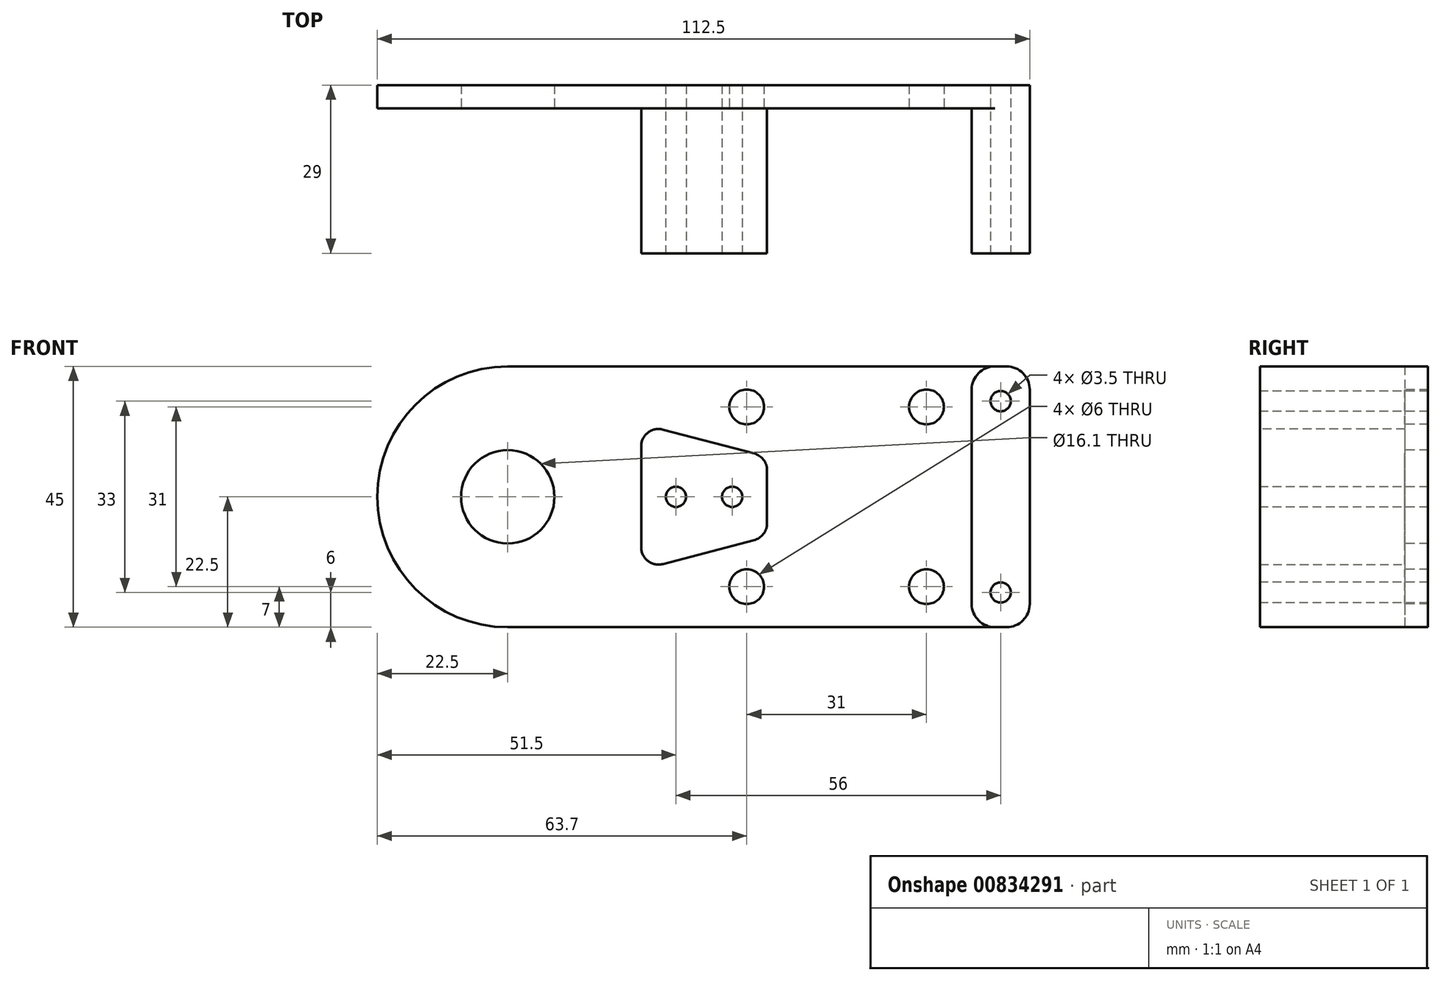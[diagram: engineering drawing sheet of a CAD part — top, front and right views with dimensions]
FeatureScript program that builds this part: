
annotation { "Feature Type Name" : "Feature", "Feature Type Description" : "" }
export const myFeature = defineFeature(function(context is Context, id is Id, definition is map)
    precondition{}
    {
        {
            var Q0;
            Q0=qCreatedBy(makeId("Front.planeOp"),FACE);
            var sketch = newSketch(context, id + "F0", { "sketchPlane" : qUnion([Q0])});
            skLineSegment(sketch, "E0.bottom", {"start": v(-45, 22.5) * mm, "end": v(45, 22.5) * mm});
            skLineSegment(sketch, "E0.top", {"start": v(-45, -22.5) * mm, "end": v(45, -22.5) * mm});
            skLineSegment(sketch, "E0.right", {"start": v(45, 22.5) * mm, "end": v(45, -22.5) * mm});
            skPoint(sketch, "E0.middle", {"position": v(0, 0) * mm});
            skArc(sketch, "E1", {"start": v(-45, 22.5) * mm, "mid": v(-67.5, 0) * mm, "end": v(-45, -22.5) * mm});
            skSolve(sketch);
        }
        {
            var Q0;
            Q0=qSketchRegion(id+"F0",true);
            extrude(context, id + "F1", {"entities" : qUnion([Q0]), "depth" : 4 * mm, "offsetDistance" : 25 * mm});
        }
        {
            var Q0;
            Q0=makeQuery(id+"F1.opExtrude","CAP_FACE",FACE,{"disambiguationData":[OSD([sQuery(id+"F0.wireOp",EDGE,"E0.bottom"),sQuery(id+"F0.wireOp",EDGE,"E0.top"),sQuery(id+"F0.wireOp",EDGE,"E0.right"),sQuery(id+"F0.wireOp",EDGE,"E1")])],"isStart":false});
            var sketch = newSketch(context, id + "F2", { "sketchPlane" : qUnion([Q0])});
            skCircle(sketch, "E2", {"center": v(-45, 0) * mm, "radius": 8.05 * mm});
            skSolve(sketch);
        }
        {
            var Q0;
            Q0 = qSketchRegion(id + "F2", true);
            extrude(context, id + "F3", {"entities" : qUnion([Q0]), "operationType" : NewBodyOperationType.REMOVE, "endBound" : BoundingType.THROUGH_ALL, "oppositeDirection" : true, "depth" : 25 * mm, "offsetDistance" : 25 * mm});
        }
        {
            var Q0;
            Q0=makeQuery(id+"F1.opExtrude","CAP_FACE",FACE,{"disambiguationData":[OSD([sQuery(id+"F0.wireOp",EDGE,"E0.bottom"),sQuery(id+"F0.wireOp",EDGE,"E0.top"),sQuery(id+"F0.wireOp",EDGE,"E0.right"),sQuery(id+"F0.wireOp",EDGE,"E1")])],"isStart":false});
            var sketch = newSketch(context, id + "F4", { "sketchPlane" : qUnion([Q0])});
            skCircle(sketch, "E3", {"center": v(-45, 0) * mm, "radius": 19.1 * mm, "construction": true});
            skLineSegment(sketch, "E4", {"start": v(-45, 0) * mm, "end": v(11.7, 0) * mm, "construction": true});
            skCircle(sketch, "E5", {"center": v(11.7, 0) * mm, "radius": 4.75 * mm, "construction": true});
            skLineSegment(sketch, "E6", {"start": v(12.9, 4.6) * mm, "end": v(-40.17, 18.48) * mm, "construction": true});
            skLineSegment(sketch, "E7", {"start": v(-40.17, -18.48) * mm, "end": v(12.9, -4.6) * mm, "construction": true});
            skLineSegment(sketch, "E8", {"start": v(-22, 12.58) * mm, "end": v(-0.3, 6.9) * mm});
            skLineSegment(sketch, "E9", {"start": v(-0.3, 6.9) * mm, "end": v(-0.3, 0) * mm});
            skLineSegment(sketch, "E10", {"start": v(-22, 12.58) * mm, "end": v(-22, 0) * mm});
            skLineSegment(sketch, "E11.MirrorCS", {"start": v(-22, -12.58) * mm, "end": v(-22, 0) * mm});
            skLineSegment(sketch, "E12.MirrorCS", {"start": v(-22, -12.58) * mm, "end": v(-0.3, -6.9) * mm});
            skLineSegment(sketch, "E13.MirrorCS", {"start": v(-0.3, -6.9) * mm, "end": v(-0.3, 0) * mm});
            skLineSegment(sketch, "E14.bottom", {"start": v(45, 22.5) * mm, "end": v(35, 22.5) * mm});
            skLineSegment(sketch, "E14.top", {"start": v(45, -22.5) * mm, "end": v(35, -22.5) * mm});
            skLineSegment(sketch, "E14.left", {"start": v(45, 22.5) * mm, "end": v(45, -22.5) * mm});
            skLineSegment(sketch, "E14.right", {"start": v(35, 22.5) * mm, "end": v(35, -22.5) * mm});
            skSolve(sketch);
        }
        {
            var Q0;
            Q0 = qSketchRegion(id + "F4", true);
            extrude(context, id + "F5", {"entities" : qUnion([Q0]), "operationType" : NewBodyOperationType.ADD, "depth" : 25 * mm, "offsetDistance" : 25 * mm});
        }
        {
            var Q0;
            Q0=makeQuery(id+"F5.opExtrude","CAP_FACE",FACE,{"disambiguationData":[OSD([sQuery(id+"F4.wireOp",EDGE,"E8"),sQuery(id+"F4.wireOp",EDGE,"E9"),sQuery(id+"F4.wireOp",EDGE,"E10"),sQuery(id+"F4.wireOp",EDGE,"E11.MirrorCS"),sQuery(id+"F4.wireOp",EDGE,"E12.MirrorCS"),sQuery(id+"F4.wireOp",EDGE,"E13.MirrorCS")])],"isStart":false});
            var sketch = newSketch(context, id + "F6", { "sketchPlane" : qUnion([Q0])});
            skLineSegment(sketch, "E15", {"start": v(-22, 0) * mm, "end": v(0, 0) * mm, "construction": true});
            skCircle(sketch, "E16", {"center": v(-16, 0) * mm, "radius": 1.75 * mm});
            skCircle(sketch, "E17", {"center": v(-6.3, 0) * mm, "radius": 1.75 * mm});
            skSolve(sketch);
        }
        {
            var Q0;
            Q0 = qSketchRegion(id + "F6", true);
            extrude(context, id + "F7", {"entities" : qUnion([Q0]), "operationType" : NewBodyOperationType.REMOVE, "endBound" : BoundingType.THROUGH_ALL, "oppositeDirection" : true, "depth" : 25 * mm, "offsetDistance" : 25 * mm});
        }
        {
            var Q0;
            Q0=makeQuery(id+"F5.opExtrude","CAP_FACE",FACE,{"disambiguationData":[OSD([sQuery(id+"F4.wireOp",EDGE,"E14.bottom"),sQuery(id+"F4.wireOp",EDGE,"E14.top"),sQuery(id+"F4.wireOp",EDGE,"E14.left"),sQuery(id+"F4.wireOp",EDGE,"E14.right")])],"isStart":false});
            var sketch = newSketch(context, id + "F8", { "sketchPlane" : qUnion([Q0])});
            skLineSegment(sketch, "E18", {"start": v(40, 22.5) * mm, "end": v(40, -22.5) * mm, "construction": true});
            skCircle(sketch, "E19", {"center": v(40, 16.5) * mm, "radius": 1.75 * mm});
            skCircle(sketch, "E20", {"center": v(40, -16.5) * mm, "radius": 1.75 * mm});
            skSolve(sketch);
        }
        {
            var Q0;
            Q0 = qSketchRegion(id + "F8", true);
            extrude(context, id + "F9", {"entities" : qUnion([Q0]), "operationType" : NewBodyOperationType.REMOVE, "endBound" : BoundingType.THROUGH_ALL, "oppositeDirection" : true, "depth" : 25 * mm, "offsetDistance" : 25 * mm});
        }
        {
            var Q0;
            Q0=makeQuery(id+"F5.opExtrude","SWEPT_EDGE",EDGE,{"disambiguationData":[OSD([sQuery(id+"F4.wireOp",EDGE,"E8"),sQuery(id+"F4.wireOp",EDGE,"E9")])]});
            var Q1;
            Q1=makeQuery(id+"F5.opExtrude","SWEPT_EDGE",EDGE,{"disambiguationData":[OSD([sQuery(id+"F4.wireOp",EDGE,"E8"),sQuery(id+"F4.wireOp",EDGE,"E10")])]});
            var Q2;
            Q2=makeQuery(id+"F5.opExtrude","SWEPT_EDGE",EDGE,{"disambiguationData":[OSD([sQuery(id+"F4.wireOp",EDGE,"E11.MirrorCS"),sQuery(id+"F4.wireOp",EDGE,"E12.MirrorCS")])]});
            var Q3;
            Q3=makeQuery(id+"F5.opExtrude","SWEPT_EDGE",EDGE,{"disambiguationData":[OSD([sQuery(id+"F4.wireOp",EDGE,"E12.MirrorCS"),sQuery(id+"F4.wireOp",EDGE,"E13.MirrorCS")])]});
            fillet(context, id + "F10", {"entities" : qUnion([Q0, Q1, Q2, Q3]), "radius" : 3 * mm, "tangentPropagation" : true, "allowEdgeOverflow" : false});
        }
        {
            var Q0;
            Q0=makeQuery(id+"F5.boolean.opBoolean","MERGE",EDGE,{"derivedFrom":[makeQuery(id+"F1.opExtrude","SWEPT_EDGE",EDGE,{"disambiguationData":[OSD([sQuery(id+"F0.wireOp",EDGE,"E0.bottom"),sQuery(id+"F0.wireOp",EDGE,"E0.right")])]}),makeQuery(id+"F5.opExtrude","SWEPT_EDGE",EDGE,{"disambiguationData":[OSD([sQuery(id+"F4.wireOp",EDGE,"E14.bottom"),sQuery(id+"F4.wireOp",EDGE,"E14.left")])]})]});
            var Q1;
            Q1=makeQuery(id+"F5.boolean.opBoolean","MERGE",EDGE,{"derivedFrom":[makeQuery(id+"F1.opExtrude","SWEPT_EDGE",EDGE,{"disambiguationData":[OSD([sQuery(id+"F0.wireOp",EDGE,"E0.top"),sQuery(id+"F0.wireOp",EDGE,"E0.right")])]}),makeQuery(id+"F5.opExtrude","SWEPT_EDGE",EDGE,{"disambiguationData":[OSD([sQuery(id+"F4.wireOp",EDGE,"E14.top"),sQuery(id+"F4.wireOp",EDGE,"E14.left")])]})]});
            var Q2;
            Q2=makeQuery(id+"F5.opExtrude","SWEPT_EDGE",EDGE,{"disambiguationData":[OSD([sQuery(id+"F0.wireOp",EDGE,"E0.bottom"),sQuery(id+"F4.wireOp",EDGE,"E14.bottom"),sQuery(id+"F4.wireOp",EDGE,"E14.right")])]});
            var Q3;
            Q3=makeQuery(id+"F5.opExtrude","SWEPT_EDGE",EDGE,{"disambiguationData":[OSD([sQuery(id+"F0.wireOp",EDGE,"E0.top"),sQuery(id+"F4.wireOp",EDGE,"E14.top"),sQuery(id+"F4.wireOp",EDGE,"E14.right")])]});
            fillet(context, id + "F11", {"entities" : qUnion([Q0, Q1, Q2, Q3]), "radius" : 4 * mm, "tangentPropagation" : true, "allowEdgeOverflow" : false});
        }
        {
            var Q0;
            Q0=makeQuery(id+"F1.opExtrude","CAP_FACE",FACE,{"disambiguationData":[OSD([sQuery(id+"F0.wireOp",EDGE,"E0.bottom"),sQuery(id+"F0.wireOp",EDGE,"E0.top"),sQuery(id+"F0.wireOp",EDGE,"E0.right"),sQuery(id+"F0.wireOp",EDGE,"E1")])],"isStart":false});
            var sketch = newSketch(context, id + "F12", { "sketchPlane" : qUnion([Q0])});
            skLineSegment(sketch, "E21", {"start": v(-45, 0) * mm, "end": v(11.7, 0) * mm, "construction": true});
            skCircle(sketch, "E22", {"center": v(-3.8, 15.5) * mm, "radius": 3 * mm});
            skCircle(sketch, "E23.1.0", {"center": v(-3.8, -15.5) * mm, "radius": 3 * mm});
            skCircle(sketch, "E23.2.0", {"center": v(27.2, -15.5) * mm, "radius": 3 * mm});
            skCircle(sketch, "E23.3.0", {"center": v(27.2, 15.5) * mm, "radius": 3 * mm});
            skPoint(sketch, "E23.center", {"position": v(11.7, 0) * mm});
            skSolve(sketch);
        }
        {
            var Q0;
            Q0 = qSketchRegion(id + "F12", true);
            extrude(context, id + "F13", {"entities" : qUnion([Q0]), "operationType" : NewBodyOperationType.REMOVE, "endBound" : BoundingType.THROUGH_ALL, "oppositeDirection" : true, "depth" : 25 * mm, "offsetDistance" : 25 * mm});
        }
    });
